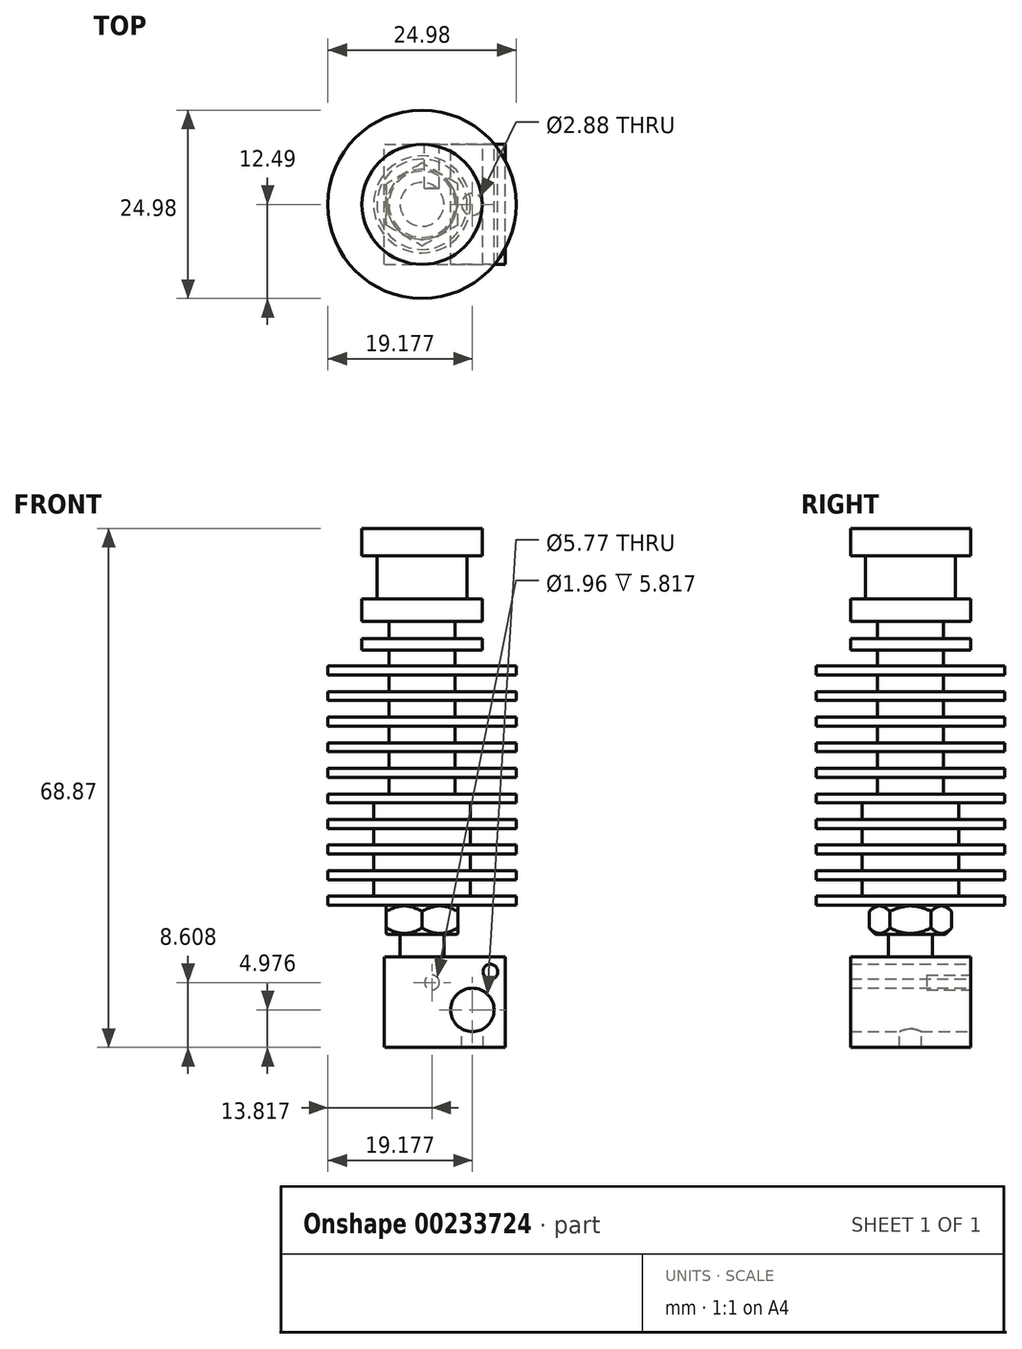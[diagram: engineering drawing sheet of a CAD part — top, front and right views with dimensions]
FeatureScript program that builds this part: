
annotation { "Feature Type Name" : "Feature", "Feature Type Description" : "" }
export const myFeature = defineFeature(function(context is Context, id is Id, definition is map)
    precondition{}
    {
        {
            var Q0;
            Q0=qCreatedBy(makeId("Front.planeOp"),FACE);
            var sketch = newSketch(context, id + "F0", { "sketchPlane" : qUnion([Q0])});
            skLineSegment(sketch, "E0", {"start": v(0, 0) * mm, "end": v(0, 50) * mm});
            skLineSegment(sketch, "E1", {"start": v(0, 50) * mm, "end": v(7.97, 50) * mm});
            skLineSegment(sketch, "E2", {"start": v(7.97, 50) * mm, "end": v(7.97, 46.35) * mm});
            skLineSegment(sketch, "E3", {"start": v(7.97, 46.35) * mm, "end": v(5.99, 46.35) * mm});
            skLineSegment(sketch, "E4", {"start": v(5.99, 46.35) * mm, "end": v(5.99, 40.61) * mm});
            skLineSegment(sketch, "E5", {"start": v(5.99, 40.61) * mm, "end": v(7.97, 40.61) * mm});
            skLineSegment(sketch, "E6", {"start": v(7.97, 40.61) * mm, "end": v(7.97, 37.66) * mm});
            skLineSegment(sketch, "E7", {"start": v(7.97, 37.66) * mm, "end": v(4.4, 37.66) * mm});
            skLineSegment(sketch, "E8", {"start": v(4.4, 37.66) * mm, "end": v(4.4, 35.38) * mm});
            skLineSegment(sketch, "E9", {"start": v(4.4, 35.38) * mm, "end": v(7.97, 35.38) * mm});
            skLineSegment(sketch, "E10", {"start": v(7.97, 35.38) * mm, "end": v(7.97, 33.86) * mm});
            skLineSegment(sketch, "E11", {"start": v(7.97, 33.86) * mm, "end": v(4.4, 33.86) * mm});
            skLineSegment(sketch, "E12", {"start": v(4.4, 33.86) * mm, "end": v(4.4, 31.72) * mm});
            skLineSegment(sketch, "E13", {"start": v(4.4, 31.72) * mm, "end": v(12.5, 31.72) * mm});
            skLineSegment(sketch, "E14", {"start": v(12.5, 31.72) * mm, "end": v(12.5, 30.54) * mm});
            skLineSegment(sketch, "E15", {"start": v(12.5, 30.54) * mm, "end": v(4.4, 30.54) * mm});
            skLineSegment(sketch, "E16", {"start": v(4.4, 30.54) * mm, "end": v(4.4, 28.33) * mm});
            skLineSegment(sketch, "E17", {"start": v(4.4, 28.33) * mm, "end": v(12.5, 28.33) * mm});
            skLineSegment(sketch, "E18", {"start": v(12.5, 28.33) * mm, "end": v(12.5, 27.15) * mm});
            skLineSegment(sketch, "E19", {"start": v(12.5, 27.15) * mm, "end": v(4.4, 27.15) * mm});
            skLineSegment(sketch, "E20", {"start": v(4.4, 27.15) * mm, "end": v(4.4, 24.94) * mm});
            skLineSegment(sketch, "E21", {"start": v(4.4, 24.94) * mm, "end": v(12.5, 24.94) * mm});
            skLineSegment(sketch, "E22", {"start": v(12.5, 24.94) * mm, "end": v(12.5, 23.76) * mm});
            skLineSegment(sketch, "E23", {"start": v(12.5, 23.76) * mm, "end": v(4.4, 23.76) * mm});
            skLineSegment(sketch, "E24", {"start": v(4.4, 23.76) * mm, "end": v(4.4, 21.54) * mm});
            skLineSegment(sketch, "E25", {"start": v(4.4, 21.54) * mm, "end": v(12.5, 21.54) * mm});
            skLineSegment(sketch, "E26", {"start": v(12.5, 21.54) * mm, "end": v(12.5, 20.36) * mm});
            skLineSegment(sketch, "E27", {"start": v(12.5, 20.36) * mm, "end": v(4.4, 20.36) * mm});
            skLineSegment(sketch, "E28", {"start": v(4.4, 20.36) * mm, "end": v(4.4, 18.15) * mm});
            skLineSegment(sketch, "E29", {"start": v(4.4, 18.15) * mm, "end": v(12.5, 18.15) * mm});
            skLineSegment(sketch, "E30", {"start": v(12.5, 18.15) * mm, "end": v(12.5, 16.97) * mm});
            skLineSegment(sketch, "E31", {"start": v(12.5, 16.97) * mm, "end": v(4.4, 16.97) * mm});
            skLineSegment(sketch, "E32", {"start": v(4.4, 16.97) * mm, "end": v(4.4, 14.76) * mm});
            skLineSegment(sketch, "E33", {"start": v(4.4, 14.76) * mm, "end": v(12.5, 14.76) * mm});
            skLineSegment(sketch, "E34", {"start": v(12.5, 14.76) * mm, "end": v(12.5, 13.57) * mm});
            skLineSegment(sketch, "E35", {"start": v(12.5, 13.57) * mm, "end": v(6.43, 13.57) * mm});
            skLineSegment(sketch, "E36", {"start": v(6.43, 13.57) * mm, "end": v(6.43, 11.36) * mm});
            skLineSegment(sketch, "E37", {"start": v(6.43, 11.36) * mm, "end": v(12.5, 11.36) * mm});
            skLineSegment(sketch, "E38", {"start": v(12.5, 11.36) * mm, "end": v(12.5, 10.18) * mm});
            skLineSegment(sketch, "E39", {"start": v(12.5, 10.18) * mm, "end": v(6.43, 10.18) * mm});
            skLineSegment(sketch, "E40", {"start": v(6.43, 10.18) * mm, "end": v(6.43, 7.97) * mm});
            skLineSegment(sketch, "E41", {"start": v(6.43, 7.97) * mm, "end": v(12.5, 7.97) * mm});
            skLineSegment(sketch, "E42", {"start": v(12.5, 7.97) * mm, "end": v(12.5, 6.79) * mm});
            skLineSegment(sketch, "E43", {"start": v(12.5, 6.79) * mm, "end": v(6.43, 6.79) * mm});
            skLineSegment(sketch, "E44", {"start": v(6.43, 6.79) * mm, "end": v(6.43, 4.57) * mm});
            skLineSegment(sketch, "E45", {"start": v(6.43, 4.57) * mm, "end": v(12.5, 4.57) * mm});
            skLineSegment(sketch, "E46", {"start": v(12.5, 4.57) * mm, "end": v(12.5, 3.4) * mm});
            skLineSegment(sketch, "E47", {"start": v(12.5, 3.4) * mm, "end": v(6.43, 3.4) * mm});
            skLineSegment(sketch, "E48", {"start": v(6.43, 3.4) * mm, "end": v(6.43, 1.18) * mm});
            skLineSegment(sketch, "E49", {"start": v(6.43, 1.18) * mm, "end": v(12.5, 1.18) * mm});
            skLineSegment(sketch, "E50", {"start": v(12.5, 1.18) * mm, "end": v(12.5, 0) * mm});
            skLineSegment(sketch, "E51", {"start": v(12.5, 0) * mm, "end": v(0, 0) * mm});
            skCircle(sketch, "E52", {"center": v(4.4, 29.44) * mm, "radius": 1.1 * mm, "construction": true});
            skCircle(sketch, "E53", {"center": v(4.4, 26.04) * mm, "radius": 1.1 * mm, "construction": true});
            skCircle(sketch, "E54", {"center": v(4.4, 22.65) * mm, "radius": 1.1 * mm, "construction": true});
            skCircle(sketch, "E55", {"center": v(4.4, 19.26) * mm, "radius": 1.1 * mm, "construction": true});
            skCircle(sketch, "E56", {"center": v(4.4, 15.86) * mm, "radius": 1.1 * mm, "construction": true});
            skLineSegment(sketch, "E57", {"start": v(6.43, 13.57) * mm, "end": v(4.4, 13.57) * mm, "construction": true});
            skLineSegment(sketch, "E58", {"start": v(4.4, 13.57) * mm, "end": v(4.4, 11.36) * mm, "construction": true});
            skLineSegment(sketch, "E59", {"start": v(4.4, 11.36) * mm, "end": v(6.43, 11.36) * mm, "construction": true});
            skLineSegment(sketch, "E60", {"start": v(6.43, 10.18) * mm, "end": v(4.4, 10.18) * mm, "construction": true});
            skLineSegment(sketch, "E61", {"start": v(4.4, 10.18) * mm, "end": v(4.4, 7.97) * mm, "construction": true});
            skLineSegment(sketch, "E62", {"start": v(4.4, 7.97) * mm, "end": v(6.43, 7.97) * mm, "construction": true});
            skLineSegment(sketch, "E63", {"start": v(6.43, 6.79) * mm, "end": v(4.4, 6.79) * mm, "construction": true});
            skLineSegment(sketch, "E64", {"start": v(4.4, 6.79) * mm, "end": v(4.4, 4.57) * mm, "construction": true});
            skLineSegment(sketch, "E65", {"start": v(4.4, 4.57) * mm, "end": v(6.43, 4.57) * mm, "construction": true});
            skLineSegment(sketch, "E66", {"start": v(6.43, 3.4) * mm, "end": v(4.4, 3.4) * mm, "construction": true});
            skLineSegment(sketch, "E67", {"start": v(4.4, 3.4) * mm, "end": v(4.4, 1.18) * mm, "construction": true});
            skLineSegment(sketch, "E68", {"start": v(4.4, 1.18) * mm, "end": v(6.43, 1.18) * mm, "construction": true});
            skCircle(sketch, "E69", {"center": v(4.4, 12.47) * mm, "radius": 1.1 * mm, "construction": true});
            skCircle(sketch, "E70", {"center": v(4.4, 9.07) * mm, "radius": 1.1 * mm, "construction": true});
            skCircle(sketch, "E71", {"center": v(4.4, 5.68) * mm, "radius": 1.1 * mm, "construction": true});
            skCircle(sketch, "E72", {"center": v(4.4, 2.29) * mm, "radius": 1.1 * mm, "construction": true});
            skLineSegment(sketch, "E73", {"start": v(4.4, 30.54) * mm, "end": v(3.3, 30.54) * mm, "construction": true});
            skLineSegment(sketch, "E74", {"start": v(3.3, 30.54) * mm, "end": v(3.3, 1.18) * mm, "construction": true});
            skLineSegment(sketch, "E75", {"start": v(3.3, 1.18) * mm, "end": v(4.4, 1.18) * mm, "construction": true});
            skCircle(sketch, "E76", {"center": v(12.5, 31.13) * mm, "radius": 0.6 * mm, "construction": true});
            skLineSegment(sketch, "E77", {"start": v(12.5, 31.72) * mm, "end": v(13.08, 31.72) * mm, "construction": true});
            skLineSegment(sketch, "E78", {"start": v(13.08, 31.72) * mm, "end": v(13.08, 0) * mm, "construction": true});
            skLineSegment(sketch, "E79", {"start": v(13.08, 0) * mm, "end": v(12.5, 0) * mm, "construction": true});
            skCircle(sketch, "E80", {"center": v(12.5, 27.74) * mm, "radius": 0.6 * mm, "construction": true});
            skCircle(sketch, "E81", {"center": v(12.5, 24.35) * mm, "radius": 0.6 * mm, "construction": true});
            skCircle(sketch, "E82", {"center": v(12.5, 20.95) * mm, "radius": 0.6 * mm, "construction": true});
            skCircle(sketch, "E83", {"center": v(12.5, 17.56) * mm, "radius": 0.6 * mm, "construction": true});
            skCircle(sketch, "E84", {"center": v(12.5, 14.17) * mm, "radius": 0.6 * mm, "construction": true});
            skCircle(sketch, "E85", {"center": v(12.5, 10.77) * mm, "radius": 0.6 * mm, "construction": true});
            skCircle(sketch, "E86", {"center": v(12.5, 7.38) * mm, "radius": 0.6 * mm, "construction": true});
            skCircle(sketch, "E87", {"center": v(12.5, 3.98) * mm, "radius": 0.6 * mm, "construction": true});
            skCircle(sketch, "E88", {"center": v(12.5, 0.6) * mm, "radius": 0.6 * mm, "construction": true});
            skLineSegment(sketch, "E89", {"start": v(4.64, 0) * mm, "end": v(5.47, -0.83) * mm});
            skLineSegment(sketch, "E90", {"start": v(5.47, -0.83) * mm, "end": v(5.47, -3.02) * mm});
            skLineSegment(sketch, "E91", {"start": v(5.47, -3.02) * mm, "end": v(4.64, -3.85) * mm});
            skLineSegment(sketch, "E92", {"start": v(4.64, -3.85) * mm, "end": v(2.91, -3.85) * mm});
            skLineSegment(sketch, "E93", {"start": v(2.91, -3.85) * mm, "end": v(2.91, -6.86) * mm});
            skLineSegment(sketch, "E94", {"start": v(2.91, -6.86) * mm, "end": v(0, -6.86) * mm});
            skLineSegment(sketch, "E95", {"start": v(0, -6.86) * mm, "end": v(0, 0) * mm});
            skLineSegment(sketch, "E96", {"start": v(5.47, -0.83) * mm, "end": v(4.64, -0.83) * mm, "construction": true});
            skLineSegment(sketch, "E97", {"start": v(4.64, -0.83) * mm, "end": v(4.64, 0) * mm, "construction": true});
            skLineSegment(sketch, "E98", {"start": v(5.47, -3.02) * mm, "end": v(4.64, -3.02) * mm, "construction": true});
            skLineSegment(sketch, "E99", {"start": v(4.64, -3.02) * mm, "end": v(4.64, -3.85) * mm, "construction": true});
            skCircle(sketch, "E100", {"center": v(4.64, -3.44) * mm, "radius": 0.41 * mm, "construction": true});
            skCircle(sketch, "E101", {"center": v(4.64, -0.41) * mm, "radius": 0.41 * mm, "construction": true});
            skLineSegment(sketch, "E102", {"start": v(4.23, -3.85) * mm, "end": v(4.23, 0) * mm, "construction": true});
            skSolve(sketch);
        }
        {
            var Q0;
            Q0=makeQuery(id+"F0.imprint","IMPRINT",FACE,{"disambiguationData":[TD([[makeQuery(id+"F0.imprint","IMPRINT",EDGE,{"derivedFrom":sQuery(id+"F0.wireOp",EDGE,"E0")}),-1.0]])]});
            var Q1;
            {var subQ0=sQuery(id+"F0.wireOp",EDGE,"E89");Q1=makeQuery(id+"F0.imprint","IMPRINT",FACE,{"disambiguationData":[TD([[makeQuery(id+"F0.imprint","IMPRINT",EDGE,{"derivedFrom":subQ0}),-1.0]])]});}
            var Q2;
            Q2=sQuery(id+"F0.wireOp",EDGE,"E0");
            revolve(context, id + "F1", {"entities" : qUnion([Q0, Q1]), "axis" : qUnion([Q2]), "revolveType" : RevolveType.FULL});
        }
        {
            var Q0;
            Q0=qCreatedBy(makeId("Top.planeOp"),FACE);
            var sketch = newSketch(context, id + "F2", { "sketchPlane" : qUnion([Q0])});
            skCircle(sketch, "E103.cCircle", {"center": v(0, 0) * mm, "radius": 5.47 * mm, "construction": true});
            skLineSegment(sketch, "E103.0", {"start": v(0, -5.47) * mm, "end": v(-4.73, -2.73) * mm});
            skLineSegment(sketch, "E103.1", {"start": v(-4.73, -2.73) * mm, "end": v(-4.73, 2.73) * mm});
            skLineSegment(sketch, "E103.2", {"start": v(-4.73, 2.73) * mm, "end": v(0, 5.47) * mm});
            skLineSegment(sketch, "E103.3", {"start": v(0, 5.47) * mm, "end": v(4.73, 2.73) * mm});
            skLineSegment(sketch, "E103.4", {"start": v(4.73, 2.73) * mm, "end": v(4.73, -2.73) * mm});
            skLineSegment(sketch, "E103.5", {"start": v(4.73, -2.73) * mm, "end": v(0, -5.47) * mm});
            skCircle(sketch, "E104.0", {"center": v(0, 0) * mm, "radius": 12.5 * mm});
            skSolve(sketch);
        }
        {
            var Q0;
            Q0=makeQuery(id+"F2.imprint","IMPRINT",FACE,{"disambiguationData":[TD([[makeQuery(id+"F2.imprint","IMPRINT",EDGE,{"derivedFrom":sQuery(id+"F2.wireOp",EDGE,"E103.0")}),1.0]])]});
            extrude(context, id + "F3", {"entities" : qUnion([Q0]), "operationType" : NewBodyOperationType.REMOVE, "oppositeDirection" : true, "depth" : 25.4 * mm});
        }
        {
            var Q0;
            Q0=makeQuery(id+"F1.opRevolve","SWEPT_FACE",FACE,{"disambiguationData":[OSD([sQuery(id+"F0.wireOp",EDGE,"E94")])]});
            cPlane(context, id + "F4", {"entities" : qUnion([Q0]), "cplaneType" : CPlaneType.OFFSET, "offset" : 0 * mm, "width" : 152.4 * mm, "height" : 152.4 * mm});
        }
        {
            var Q0;
            Q0=qCreatedBy(id+"F4.planeOp",FACE);
            var sketch = newSketch(context, id + "F5", { "sketchPlane" : qUnion([Q0])});
            skLineSegment(sketch, "E105.bottom", {"start": v(-4.98, 7.97) * mm, "end": v(11.03, 7.97) * mm});
            skLineSegment(sketch, "E105.top", {"start": v(-4.98, -7.97) * mm, "end": v(11.03, -7.97) * mm});
            skLineSegment(sketch, "E105.left", {"start": v(-4.98, 7.97) * mm, "end": v(-4.98, -7.97) * mm});
            skLineSegment(sketch, "E105.right", {"start": v(11.03, 7.97) * mm, "end": v(11.03, -7.97) * mm});
            skLineSegment(sketch, "E106", {"start": v(-4.98, 0) * mm, "end": v(11.03, 0) * mm, "construction": true});
            skSolve(sketch);
        }
        {
            var Q0;
            Q0 = qSketchRegion(id + "F5", true);
            extrude(context, id + "F6", {"entities" : qUnion([Q0]), "operationType" : NewBodyOperationType.ADD, "depth" : 12 * mm});
        }
        {
            var Q0;
            Q0=makeQuery(id+"F6.opExtrude","SWEPT_FACE",FACE,{"disambiguationData":[OSD([sQuery(id+"F5.wireOp",EDGE,"E105.top")])]});
            var sketch = newSketch(context, id + "F7", { "sketchPlane" : qUnion([Q0])});
            skCircle(sketch, "E107", {"center": v(-6.69, -13.9) * mm, "radius": 2.88 * mm});
            skCircle(sketch, "E108", {"center": v(-1.33, -10.26) * mm, "radius": 0.98 * mm});
            skCircle(sketch, "E109", {"center": v(-9.07, -8.81) * mm, "radius": 0.98 * mm});
            skSolve(sketch);
        }
        {
            var Q0;
            Q0=makeQuery(id+"F7.imprint","IMPRINT",FACE,{"disambiguationData":[TD([[makeQuery(id+"F7.imprint","IMPRINT",EDGE,{"derivedFrom":sQuery(id+"F7.wireOp",EDGE,"E107")}),1.0]])]});
            var Q1;
            Q1=makeQuery(id+"F7.imprint","IMPRINT",FACE,{"disambiguationData":[TD([[makeQuery(id+"F7.imprint","IMPRINT",EDGE,{"derivedFrom":sQuery(id+"F7.wireOp",EDGE,"E109")}),1.0]])]});
            extrude(context, id + "F8", {"entities" : qUnion([Q0, Q1]), "operationType" : NewBodyOperationType.REMOVE, "oppositeDirection" : true, "depth" : 25.4 * mm});
        }
        {
            var Q0;
            Q0=makeQuery(id+"F7.imprint","IMPRINT",FACE,{"disambiguationData":[TD([[makeQuery(id+"F7.imprint","IMPRINT",EDGE,{"derivedFrom":sQuery(id+"F7.wireOp",EDGE,"E108")}),1.0]])]});
            extrude(context, id + "F9", {"entities" : qUnion([Q0]), "operationType" : NewBodyOperationType.REMOVE, "oppositeDirection" : true, "depth" : 5.82 * mm});
        }
        {
            var Q0;
            Q0=makeQuery(id+"F6.opExtrude","CAP_FACE",FACE,{"disambiguationData":[OSD([sQuery(id+"F5.wireOp",EDGE,"E105.bottom"),sQuery(id+"F5.wireOp",EDGE,"E105.top"),sQuery(id+"F5.wireOp",EDGE,"E105.left"),sQuery(id+"F5.wireOp",EDGE,"E105.right")])],"isStart":false});
            var Q1;
            Q1=sQuery(id+"F7.wireOp",VERTEX,"E107.center");
            cPlane(context, id + "F10", {"entities" : qUnion([Q0, Q1]), "cplaneType" : CPlaneType.PLANE_POINT, "offset" : 25.4 * mm, "width" : 152.4 * mm, "height" : 152.4 * mm});
        }
        {
            var Q0;
            Q0=qCreatedBy(id+"F10.planeOp",FACE);
            var sketch = newSketch(context, id + "F11", { "sketchPlane" : qUnion([Q0])});
            skLineSegment(sketch, "E110.0.0", {"start": v(9.57, -7.97) * mm, "end": v(3.8, -7.97) * mm, "construction": true});
            skLineSegment(sketch, "E111.0", {"start": v(3.8, 7.97) * mm, "end": v(9.57, 7.97) * mm, "construction": true});
            skLineSegment(sketch, "E112", {"start": v(9.57, -7.97) * mm, "end": v(9.57, 7.97) * mm, "construction": true});
            skLineSegment(sketch, "E113", {"start": v(3.8, -7.97) * mm, "end": v(3.8, 7.97) * mm, "construction": true});
            skLineSegment(sketch, "E114", {"start": v(6.69, 7.97) * mm, "end": v(6.69, -7.97) * mm, "construction": true});
            skCircle(sketch, "E115", {"center": v(6.69, 0) * mm, "radius": 1.44 * mm});
            skSolve(sketch);
        }
        {
            var Q0;
            Q0 = qSketchRegion(id + "F11", true);
            extrude(context, id + "F12", {"entities" : qUnion([Q0]), "operationType" : NewBodyOperationType.REMOVE, "depth" : 25.4 * mm});
        }
    });
